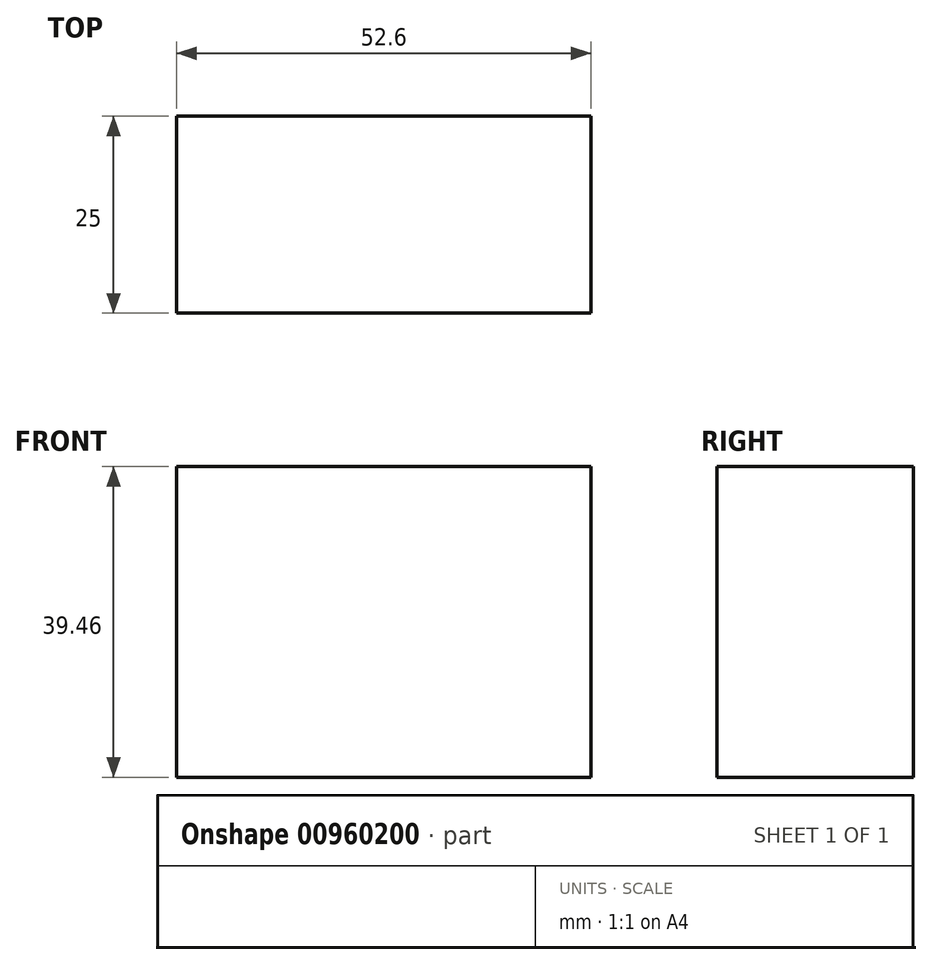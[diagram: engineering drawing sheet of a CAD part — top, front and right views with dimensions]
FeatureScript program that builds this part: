
annotation { "Feature Type Name" : "Feature", "Feature Type Description" : "" }
export const myFeature = defineFeature(function(context is Context, id is Id, definition is map)
    precondition{}
    {
        {
            var Q0;
            Q0=qCreatedBy(makeId("Front.planeOp"),FACE);
            var sketch = newSketch(context, id + "F0", { "sketchPlane" : qUnion([Q0])});
            skLineSegment(sketch, "E0.bottom", {"start": v(-59.76, 69.69) * mm, "end": v(-7.16, 69.69) * mm});
            skLineSegment(sketch, "E0.top", {"start": v(-59.76, 30.23) * mm, "end": v(-7.16, 30.23) * mm});
            skLineSegment(sketch, "E0.left", {"start": v(-59.76, 69.69) * mm, "end": v(-59.76, 30.23) * mm});
            skLineSegment(sketch, "E0.right", {"start": v(-7.16, 69.69) * mm, "end": v(-7.16, 30.23) * mm});
            skSolve(sketch);
        }
        {
            var Q0;
            Q0 = qSketchRegion(id + "F0", true);
            extrude(context, id + "F1", {"entities" : qUnion([Q0]), "depth" : 25 * mm, "offsetDistance" : 25 * mm});
        }
    });
